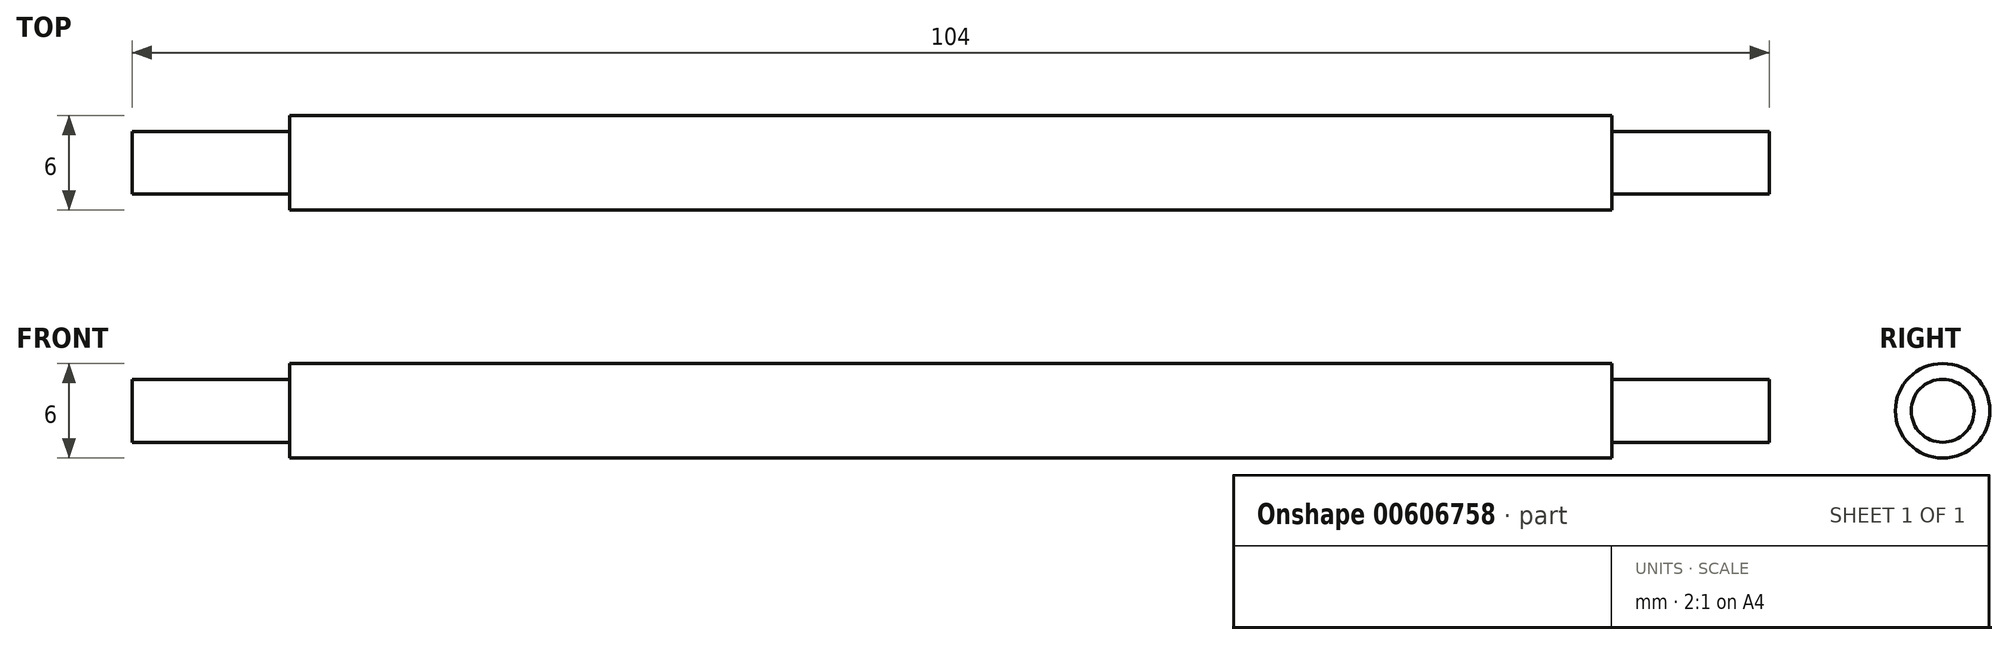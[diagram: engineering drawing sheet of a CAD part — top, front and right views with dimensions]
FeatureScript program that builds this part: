
annotation { "Feature Type Name" : "Feature", "Feature Type Description" : "" }
export const myFeature = defineFeature(function(context is Context, id is Id, definition is map)
    precondition{}
    {
        {
            var Q0;
            Q0=qCreatedBy(makeId("Front.planeOp"),FACE);
            var sketch = newSketch(context, id + "F0", { "sketchPlane" : qUnion([Q0])});
            skLineSegment(sketch, "E0", {"start": v(0, 0) * mm, "end": v(0, 2) * mm});
            skLineSegment(sketch, "E1", {"start": v(0, 2) * mm, "end": v(10, 2) * mm});
            skLineSegment(sketch, "E2", {"start": v(10, 2) * mm, "end": v(10, 3) * mm});
            skLineSegment(sketch, "E3", {"start": v(10, 3) * mm, "end": v(94, 3) * mm});
            skLineSegment(sketch, "E4", {"start": v(94, 3) * mm, "end": v(94, 2) * mm});
            skLineSegment(sketch, "E5", {"start": v(94, 2) * mm, "end": v(104, 2) * mm});
            skLineSegment(sketch, "E6", {"start": v(104, 2) * mm, "end": v(104, 0) * mm});
            skLineSegment(sketch, "E7", {"start": v(104, 0) * mm, "end": v(0, 0) * mm});
            skSolve(sketch);
        }
        {
            var Q0;
            Q0=makeQuery(id+"F0.imprint","IMPRINT",FACE,{"disambiguationData":[TD([[makeQuery(id+"F0.imprint","IMPRINT",EDGE,{"derivedFrom":sQuery(id+"F0.wireOp",EDGE,"E0")}),-1.0]])]});
            var Q1;
            Q1=sQuery(id+"F0.wireOp",EDGE,"E7");
            revolve(context, id + "F1", {"entities" : qUnion([Q0]), "axis" : qUnion([Q1]), "revolveType" : RevolveType.FULL});
        }
    });
